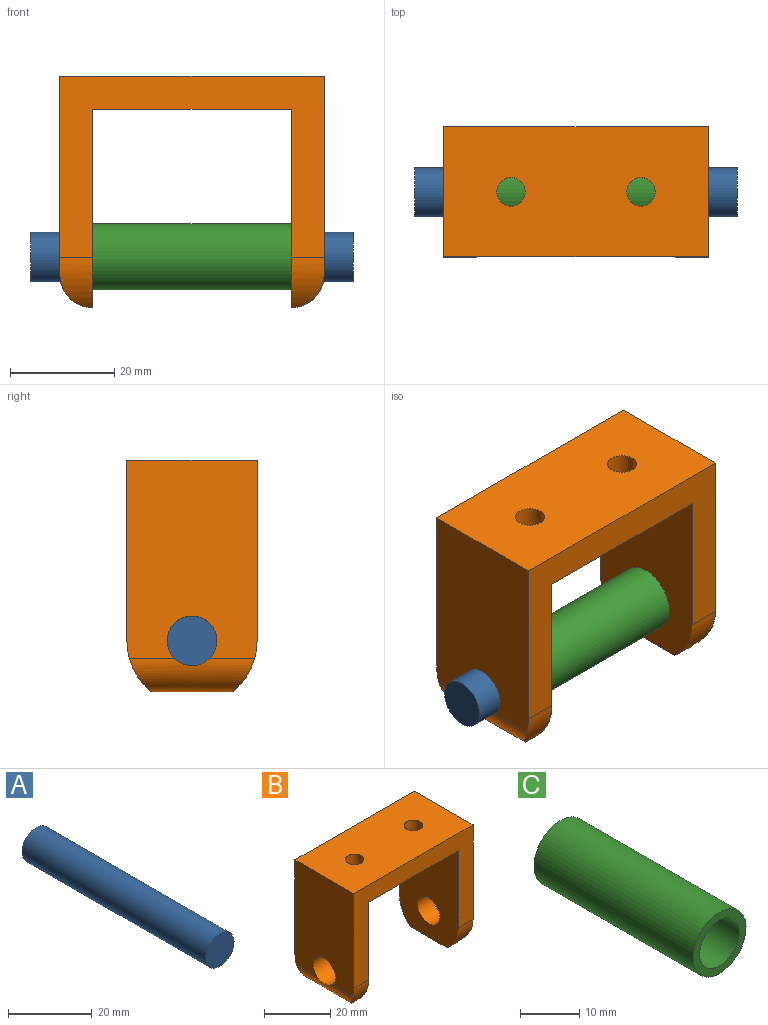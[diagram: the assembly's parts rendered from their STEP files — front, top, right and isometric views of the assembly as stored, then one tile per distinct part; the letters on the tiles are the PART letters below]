
ASSEMBLY  parts=3 mates=2
PART A: 3 faces, bbox 9.5x62x9.5 mm
  f0: cylinder r=4.76mm len=62mm, axis (0,1,0), area 1855.3mm2, adj f1,f2
  f1: plane 9.53x9.53mm, normal (0,-1,0), area 71.3mm2, adj f0
  f2: plane 9.53x9.53mm, normal (0,1,0), area 71.3mm2, adj f0
PART B: 18 faces, bbox 50.8x25x44.5 mm
  f0: cylinder r=6.35mm len=24.05mm, axis (0,1,0), area 188.7mm2, adj f1,f2,f11,f14,f15
  f1: plane 38.11x25.01mm, normal (1,0,0), area 886.4mm2, adj f0,f3,f7,f9,f11,f14,f15
  f2: plane 38.1x25mm, normal (-1,0,0), area 853.5mm2, adj f0,f3,f8,f9,f11,f14,f15
  f3: plane 50.8x34.86mm, normal (0,-1,0), area 684.6mm2, adj f1,f2,f5,f6,f7,f8,f12,f15
  f4: cylinder r=6.35mm len=24.05mm, axis (0,1,0), area 191.6mm2, adj f5,f6,f10,f12,f13
  f5: plane 38.1x25mm, normal (-1,0,0), area 886.4mm2, adj f3,f4,f7,f9,f10,f12,f13
  f6: plane 38.1x25mm, normal (1,0,0), area 853.5mm2, adj f3,f4,f8,f9,f10,f12,f13
  f7: plane 50.8x25mm, normal (0,0,1), area 1222.5mm2, adj f1,f3,f5,f9,f16,f17
  f8: plane 38.1x25mm, normal (0,0,-1), area 905mm2, adj f2,f3,f6,f9,f16,f17
  f9: plane 50.8x34.86mm, normal (0,1,0), area 684.6mm2, adj f1,f2,f5,f6,f7,f8,f13,f14
  f10: cylinder r=4.76mm len=9.53mm, axis (1,0,0), area 190mm2, adj f4,f5,f6
  f11: cylinder r=4.76mm len=9.53mm, axis (1,0,0), area 189.2mm2, adj f0,f1,f2
  f12: cylinder r=12.5mm len=9.59mm, axis (1,0,0), area 58.2mm2, adj f3,f4,f5,f6
  f13: cylinder r=12.5mm len=9.59mm, axis (1,0,0), area 58.2mm2, adj f4,f5,f6,f9
  f14: cylinder r=12.5mm len=9.59mm, axis (1,0,0), area 58.2mm2, adj f0,f1,f2,f9
  f15: cylinder r=12.5mm len=9.59mm, axis (1,0,0), area 58.2mm2, adj f0,f1,f2,f3
  f16: cylinder r=2.75mm len=6.35mm, axis (0,0,-1), area 109.7mm2, adj f7,f8
  f17: cylinder r=2.75mm len=6.35mm, axis (0,0,-1), area 109.7mm2, adj f7,f8
PART C: 4 faces, bbox 12.7x38.1x12.7 mm
  f0: cylinder r=4.76mm len=38.1mm, axis (0,1,0), area 1140.1mm2, adj f2,f3
  f1: cylinder r=6.35mm len=38.1mm, axis (0,1,0), area 1520.1mm2, adj f2,f3
  f2: plane 12.7x12.7mm, normal (0,-1,0), area 55.4mm2, adj f0,f1
  f3: plane 12.7x12.7mm, normal (0,1,0), area 55.4mm2, adj f0,f1
PLACE A rot(axis=(-0.58,-0.58,-0.58),120deg) t=(0,0,-34.69)mm
PLACE B at identity
PLACE C rot(axis=(0.58,0.58,-0.58),120deg) t=(0,0,-34.69)mm
MATE revolute C.f1 <-> A.f0  axis (1,0,0) through (0,0,-34.69)mm
MATE revolute C.f0 <-> B.f12  axis (1,0,0) through (-19.05,0,-34.69)mm
